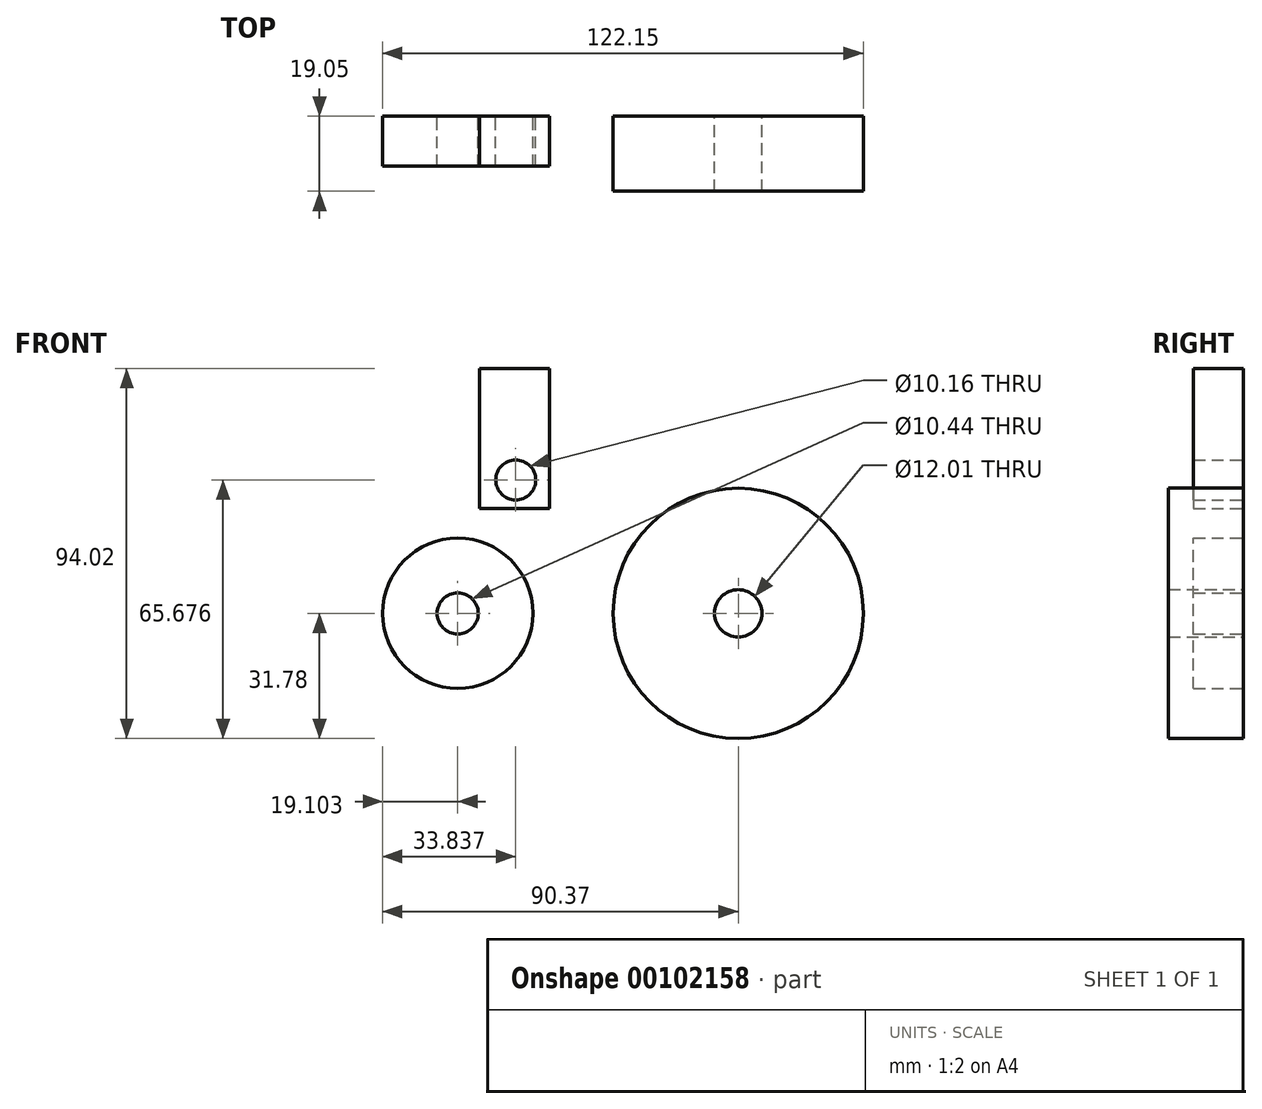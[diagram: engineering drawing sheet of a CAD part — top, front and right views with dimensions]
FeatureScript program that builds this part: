
annotation { "Feature Type Name" : "Feature", "Feature Type Description" : "" }
export const myFeature = defineFeature(function(context is Context, id is Id, definition is map)
    precondition{}
    {
        {
            var Q0;
            Q0=qCreatedBy(makeId("Front.planeOp"),FACE);
            var sketch = newSketch(context, id + "F0", { "sketchPlane" : qUnion([Q0])});
            skCircle(sketch, "E0", {"center": v(0, 0) * mm, "radius": 31.78 * mm});
            skCircle(sketch, "E1", {"center": v(0, 0) * mm, "radius": 6 * mm});
            skSolve(sketch);
        }
        {
            var Q0;
            Q0 = qSketchRegion(id + "F0", true);
            extrude(context, id + "F1", {"entities" : qUnion([Q0]), "depth" : 19.05 * mm});
        }
        {
            var Q0;
            Q0=qCreatedBy(makeId("Front.planeOp"),FACE);
            var sketch = newSketch(context, id + "F2", { "sketchPlane" : qUnion([Q0])});
            skCircle(sketch, "E2", {"center": v(-71.27, 0) * mm, "radius": 19.1 * mm});
            skCircle(sketch, "E3", {"center": v(-71.27, 0) * mm, "radius": 5.22 * mm});
            skSolve(sketch);
        }
        {
            var Q0;
            Q0 = qSketchRegion(id + "F2", true);
            extrude(context, id + "F3", {"entities" : qUnion([Q0]), "depth" : 12.7 * mm});
        }
        {
            var Q0;
            Q0=qCreatedBy(makeId("Front.planeOp"),FACE);
            var sketch = newSketch(context, id + "F4", { "sketchPlane" : qUnion([Q0])});
            skLineSegment(sketch, "E4.bottom", {"start": v(-65.78, 62.24) * mm, "end": v(-48, 62.24) * mm});
            skLineSegment(sketch, "E4.top", {"start": v(-65.78, 26.68) * mm, "end": v(-48, 26.68) * mm});
            skLineSegment(sketch, "E4.left", {"start": v(-65.78, 62.24) * mm, "end": v(-65.78, 26.68) * mm});
            skLineSegment(sketch, "E4.right", {"start": v(-48, 62.24) * mm, "end": v(-48, 26.68) * mm});
            skLineSegment(sketch, "E5", {"start": v(-65.78, 26.68) * mm, "end": v(-56.9, 26.68) * mm});
            skCircle(sketch, "E6", {"center": v(-56.53, 33.9) * mm, "radius": 5.08 * mm});
            skLineSegment(sketch, "E7", {"start": v(-56.9, 26.68) * mm, "end": v(-56.53, 62.24) * mm});
            skPoint(sketch, "E7.endSnap0", {"position": v(-56.9, 62.24) * mm});
            skSolve(sketch);
        }
        {
            var Q0;
            Q0 = qSketchRegion(id + "F4", true);
            extrude(context, id + "F5", {"entities" : qUnion([Q0]), "depth" : 12.7 * mm});
        }
    });
